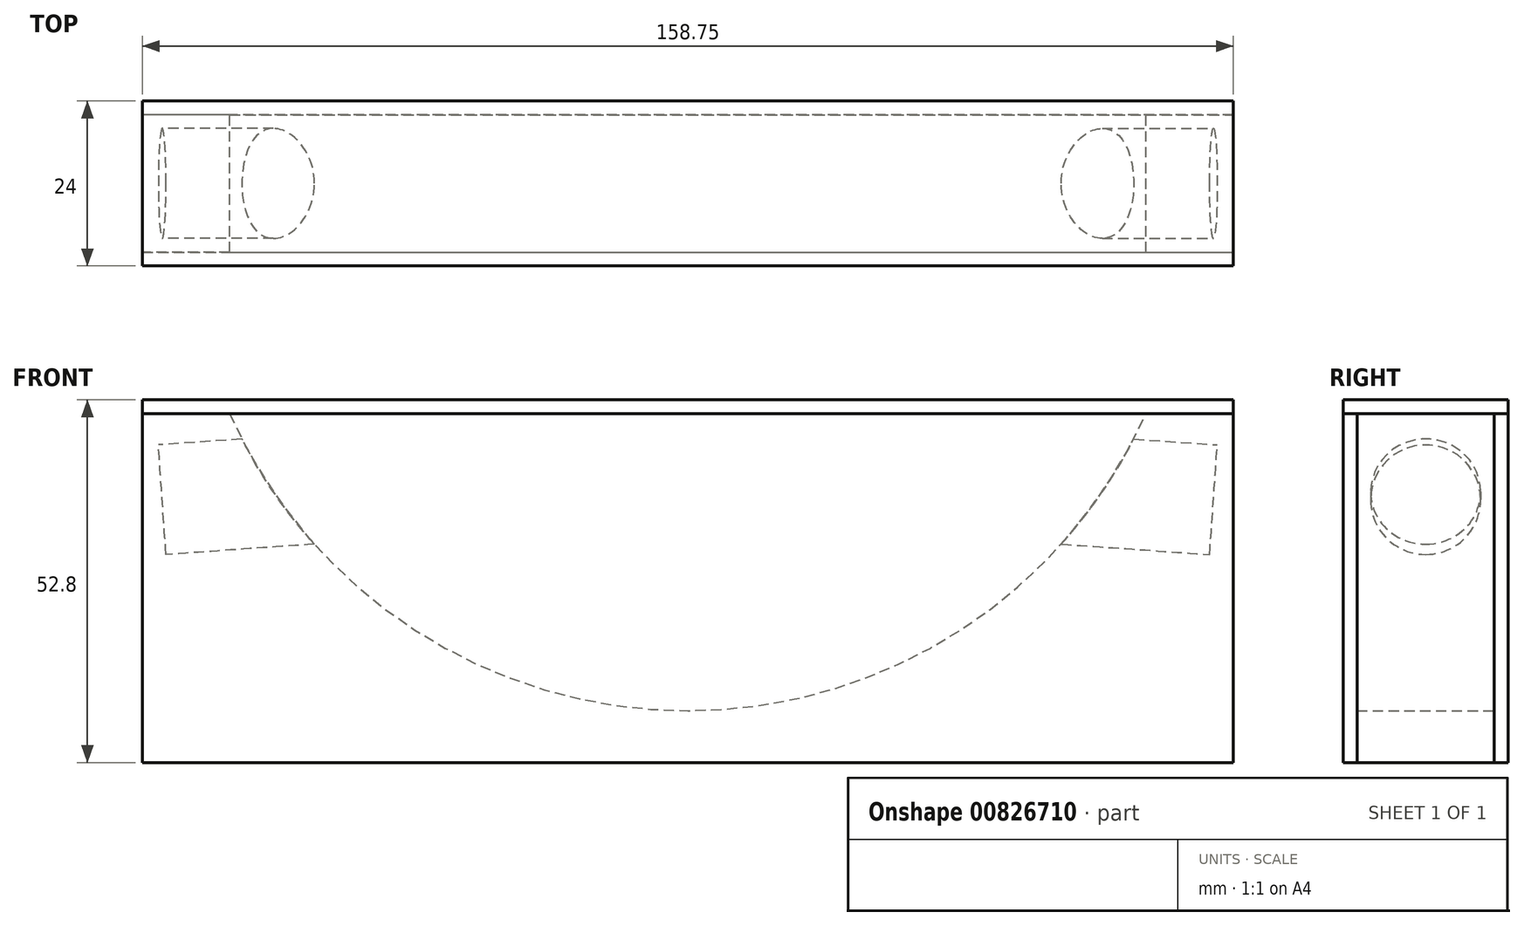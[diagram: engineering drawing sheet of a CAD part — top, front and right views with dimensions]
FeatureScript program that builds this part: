
annotation { "Feature Type Name" : "Feature", "Feature Type Description" : "" }
export const myFeature = defineFeature(function(context is Context, id is Id, definition is map)
    precondition{}
    {
        {
            var Q0;
            Q0=qCreatedBy(makeId("Front.planeOp"),FACE);
            var sketch = newSketch(context, id + "F0", { "sketchPlane" : qUnion([Q0])});
            skLineSegment(sketch, "E0.top", {"start": v(19, -33.73) * mm, "end": v(98.37, -33.73) * mm});
            skLineSegment(sketch, "E0.right", {"start": v(98.37, 17.07) * mm, "end": v(98.37, -33.73) * mm});
            skLineSegment(sketch, "E1", {"start": v(19, -33.73) * mm, "end": v(19, 72.38) * mm, "construction": true});
            skArc(sketch, "E2", {"start": v(19, -26.17) * mm, "mid": v(58.73, -14.41) * mm, "end": v(85.67, 17.07) * mm});
            skLineSegment(sketch, "E3.trimOffspring", {"start": v(85.67, 17.07) * mm, "end": v(98.37, 17.07) * mm});
            skPoint(sketch, "E0.left.end.orphan", {"position": v(-60.38, -33.73) * mm});
            skLineSegment(sketch, "E4", {"start": v(19, -26.17) * mm, "end": v(19, -33.73) * mm});
            skSolve(sketch);
        }
        {
            var Q0;
            Q0=makeQuery(id+"F0.imprint","IMPRINT",FACE,{"disambiguationData":[TD([[makeQuery(id+"F0.imprint","IMPRINT",EDGE,{"derivedFrom":sQuery(id+"F0.wireOp",EDGE,"E0.bottom")}),-1.0]])]});
            var Q1;
            Q1=makeQuery(id+"F0.imprint","IMPRINT",FACE,{"disambiguationData":[TD([[makeQuery(id+"F0.imprint","IMPRINT",EDGE,{"derivedFrom":sQuery(id+"F0.wireOp",EDGE,"E0.top")}),1.0]])]});
            extrude(context, id + "F1", {"entities" : qUnion([Q0, Q1]), "depth" : 20 * mm, "offsetDistance" : 25 * mm});
        }
        {
            var Q0;
            Q0=makeQuery(id+"F1.opExtrude","SWEPT_EDGE",EDGE,{"disambiguationData":[OSD([sQuery(id+"F0.wireOp",EDGE,"E0.right"),sQuery(id+"F0.wireOp",EDGE,"E3.trimOffspring")])]});
            cPlane(context, id + "F2", {"entities" : qUnion([Q0]), "cplaneType" : CPlaneType.LINE_ANGLE, "offset" : 25 * mm, "angle" : 94 * degree, "width" : 150 * mm, "height" : 150 * mm});
        }
        {
            var Q0;
            Q0=qCreatedBy(id+"F2.planeOp",FACE);
            var sketch = newSketch(context, id + "F3", { "sketchPlane" : qUnion([Q0])});
            skLineSegment(sketch, "E5.0", {"start": v(-20, 23.9) * mm, "end": v(0, 23.9) * mm, "construction": true});
            skLineSegment(sketch, "E6", {"start": v(-10, 23.9) * mm, "end": v(-10, 28.63) * mm, "construction": true});
            skLineSegment(sketch, "E7", {"start": v(-10, 23.9) * mm, "end": v(-10, 11.2) * mm, "construction": true});
            skCircle(sketch, "E8", {"center": v(-10, 11.2) * mm, "radius": 8 * mm});
            skSolve(sketch);
        }
        {
            var Q0;
            Q0=qCreatedBy(id+"F2.planeOp",FACE);
            cPlane(context, id + "F4", {"entities" : qUnion([Q0]), "cplaneType" : CPlaneType.OFFSET, "offset" : 2 * mm, "oppositeDirection" : true, "width" : 150 * mm, "height" : 150 * mm});
        }
        {
            var Q0;
            Q0=qCreatedBy(id+"F4.planeOp",FACE);
            var sketch = newSketch(context, id + "F5", { "sketchPlane" : qUnion([Q0])});
            skCircle(sketch, "E9.0", {"center": v(-10, 11.2) * mm, "radius": 8 * mm});
            skSolve(sketch);
        }
        {
            var Q0;
            Q0 = qSketchRegion(id + "F5", true);
            extrude(context, id + "F6", {"entities" : qUnion([Q0]), "operationType" : NewBodyOperationType.REMOVE, "endBound" : BoundingType.UP_TO_NEXT, "oppositeDirection" : true, "depth" : 25 * mm, "offsetDistance" : 25 * mm});
        }
        {
            var Q0;
            Q0=makeQuery(id+"F1.opExtrude","SWEPT_BODY",BODY,{"disambiguationData":[OSD([sQuery(id+"F0.wireOp",EDGE,"E0.top"),sQuery(id+"F0.wireOp",EDGE,"E0.right"),sQuery(id+"F0.wireOp",EDGE,"E2"),sQuery(id+"F0.wireOp",EDGE,"E3.trimOffspring"),sQuery(id+"F0.wireOp",EDGE,"E4")])]});
            var Q1;
            Q1=makeQuery(id+"F1.opExtrude","SWEPT_FACE",FACE,{"disambiguationData":[OSD([sQuery(id+"F0.wireOp",EDGE,"E4")])]});
            mirror(context, id + "F7", {"operationType" : NewBodyOperationType.ADD, "entities" : qUnion([Q0]), "mirrorPlane" : qUnion([Q1])});
        }
        {
            var Q0;
            {var subQ0=makeQuery(id+"F1.opExtrude","CAP_FACE",FACE,{"disambiguationData":[OSD([sQuery(id+"F0.wireOp",EDGE,"E0.top"),sQuery(id+"F0.wireOp",EDGE,"E0.right"),sQuery(id+"F0.wireOp",EDGE,"E2"),sQuery(id+"F0.wireOp",EDGE,"E3.trimOffspring"),sQuery(id+"F0.wireOp",EDGE,"E4")])],"isStart":true});Q0=makeQuery(id+"F7.boolean.opBoolean","MERGE",FACE,{"derivedFrom":[subQ0,makeQuery(id+"F7.opPattern","COPY",FACE,{"derivedFrom":subQ0,"instanceName":"1"})]});}
            var sketch = newSketch(context, id + "F8", { "sketchPlane" : qUnion([Q0])});
            skPoint(sketch, "E10.0", {"position": v(-98.37, 17.07) * mm});
            skPoint(sketch, "E11.0", {"position": v(60.38, -33.73) * mm});
            skLineSegment(sketch, "E12.bottom", {"start": v(-98.37, 17.07) * mm, "end": v(60.38, 17.07) * mm});
            skLineSegment(sketch, "E12.top", {"start": v(-98.37, -33.73) * mm, "end": v(60.38, -33.73) * mm});
            skLineSegment(sketch, "E12.left", {"start": v(-98.37, 17.07) * mm, "end": v(-98.37, -33.73) * mm});
            skLineSegment(sketch, "E12.right", {"start": v(60.38, 17.07) * mm, "end": v(60.38, -33.73) * mm});
            skSolve(sketch);
        }
        {
            var Q0;
            Q0 = qSketchRegion(id + "F8", true);
            extrude(context, id + "F9", {"entities" : qUnion([Q0]), "depth" : 2 * mm, "offsetDistance" : 25 * mm});
        }
        {
            var Q0;
            {var subQ0=makeQuery(id+"F1.opExtrude","CAP_FACE",FACE,{"disambiguationData":[OSD([sQuery(id+"F0.wireOp",EDGE,"E0.top"),sQuery(id+"F0.wireOp",EDGE,"E0.right"),sQuery(id+"F0.wireOp",EDGE,"E2"),sQuery(id+"F0.wireOp",EDGE,"E3.trimOffspring"),sQuery(id+"F0.wireOp",EDGE,"E4")])],"isStart":false});Q0=makeQuery(id+"F7.boolean.opBoolean","MERGE",FACE,{"derivedFrom":[subQ0,makeQuery(id+"F7.opPattern","COPY",FACE,{"derivedFrom":subQ0,"instanceName":"1"})]});}
            var sketch = newSketch(context, id + "F10", { "sketchPlane" : qUnion([Q0])});
            skPoint(sketch, "E13.0", {"position": v(-60.38, 17.07) * mm});
            skPoint(sketch, "E14.0", {"position": v(98.37, -33.73) * mm});
            skLineSegment(sketch, "E15.bottom", {"start": v(-60.38, 17.07) * mm, "end": v(98.37, 17.07) * mm});
            skLineSegment(sketch, "E15.top", {"start": v(-60.38, -33.73) * mm, "end": v(98.37, -33.73) * mm});
            skLineSegment(sketch, "E15.left", {"start": v(-60.38, 17.07) * mm, "end": v(-60.38, -33.73) * mm});
            skLineSegment(sketch, "E15.right", {"start": v(98.37, 17.07) * mm, "end": v(98.37, -33.73) * mm});
            skSolve(sketch);
        }
        {
            var Q0;
            Q0 = qSketchRegion(id + "F10", true);
            extrude(context, id + "F11", {"entities" : qUnion([Q0]), "depth" : 2 * mm, "offsetDistance" : 25 * mm});
        }
        {
            var Q0;
            Q0=makeQuery(id+"F7.opPattern","COPY",FACE,{"derivedFrom":makeQuery(id+"F1.opExtrude","SWEPT_FACE",FACE,{"disambiguationData":[OSD([sQuery(id+"F0.wireOp",EDGE,"E3.trimOffspring")])]}),"instanceName":"1"});
            var sketch = newSketch(context, id + "F12", { "sketchPlane" : qUnion([Q0])});
            skPoint(sketch, "E16.0", {"position": v(-60.38, 2) * mm});
            skPoint(sketch, "E17.0", {"position": v(98.37, -22) * mm});
            skLineSegment(sketch, "E18.bottom", {"start": v(-60.38, 2) * mm, "end": v(98.37, 2) * mm});
            skLineSegment(sketch, "E18.top", {"start": v(-60.38, -22) * mm, "end": v(98.37, -22) * mm});
            skLineSegment(sketch, "E18.left", {"start": v(-60.38, 2) * mm, "end": v(-60.38, -22) * mm});
            skLineSegment(sketch, "E18.right", {"start": v(98.37, 2) * mm, "end": v(98.37, -22) * mm});
            skSolve(sketch);
        }
        {
            var Q0;
            Q0 = qSketchRegion(id + "F12", true);
            extrude(context, id + "F13", {"entities" : qUnion([Q0]), "depth" : 2 * mm, "offsetDistance" : 25 * mm});
        }
    });
